# Revit family: 11Construction_Fences-&-Traffic-Security_AutoGate_Barracuda-Pivot-Gates
name_source: partatom
category: Specialty Equipment
units: mm (PartAtom-declared; Revit-internal decimal feet)

## family parameters
Always vertical = Yes
Cut with Voids When Loaded = No
Enable Cutting in Views = Yes
Maintain Annotation Orientation = No
OmniClass Number = 23.25.40.21.21
OmniClass Title = Gates
Part Type = Normal
Room Calculation Point = No
Round Connector Dimension = Use Diameter
Shared = No
Work Plane-Based = Yes

## types (1)
- Barracuda VPG
    Assembly Code = G2040100
    Date Updated = -
    Default Elevation = 0 "
    Description = Barracuda Vertical Pivot Gate
    Installation instructions = https://www.itwredhead.com
    Keynote = 323100
    Manufacturer = AutoGate
    Model = Barracuda VPG
    Product Documentation Link = https://www.itwredhead.com
    Product Page URL = https://www.autogate.com
    Product data url = https://www.bimobject.com
    URL = https://www.autogate.com
    Version = 1

## geometry (parser evidence)
native form markers: Sweep x10
no freeform markers — native parametric forms only
